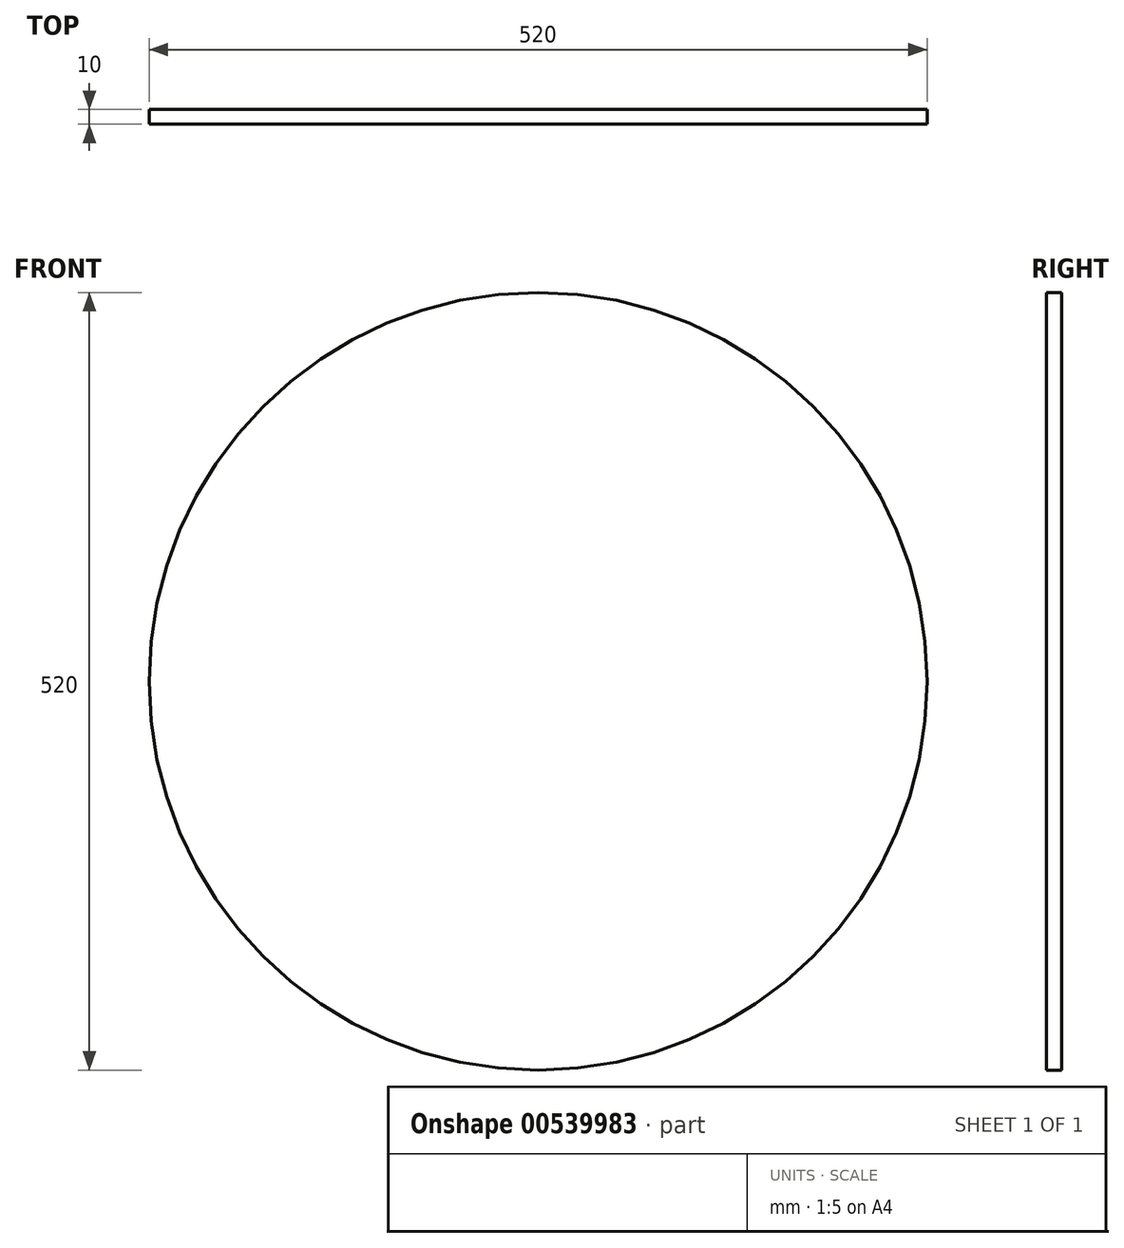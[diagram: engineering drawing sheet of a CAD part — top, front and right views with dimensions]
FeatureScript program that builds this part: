
annotation { "Feature Type Name" : "Feature", "Feature Type Description" : "" }
export const myFeature = defineFeature(function(context is Context, id is Id, definition is map)
    precondition{}
    {
        {
            var Q0;
            Q0=qCreatedBy(makeId("Front.planeOp"),FACE);
            var sketch = newSketch(context, id + "F0", { "sketchPlane" : qUnion([Q0])});
            skCircle(sketch, "E0.0", {"center": v(0, 0) * mm, "radius": 260 * mm});
            skSolve(sketch);
        }
        {
            var Q0;
            Q0=makeQuery(id+"F0.imprint","IMPRINT",FACE,{"disambiguationData":[TD([[makeQuery(id+"F0.imprint","IMPRINT",EDGE,{"derivedFrom":sQuery(id+"F0.wireOp",EDGE,"E0.0")}),1.0]])]});
            extrude(context, id + "F1", {"entities" : qUnion([Q0]), "depth" : 10 * mm, "offsetDistance" : 25 * mm});
        }
    });
